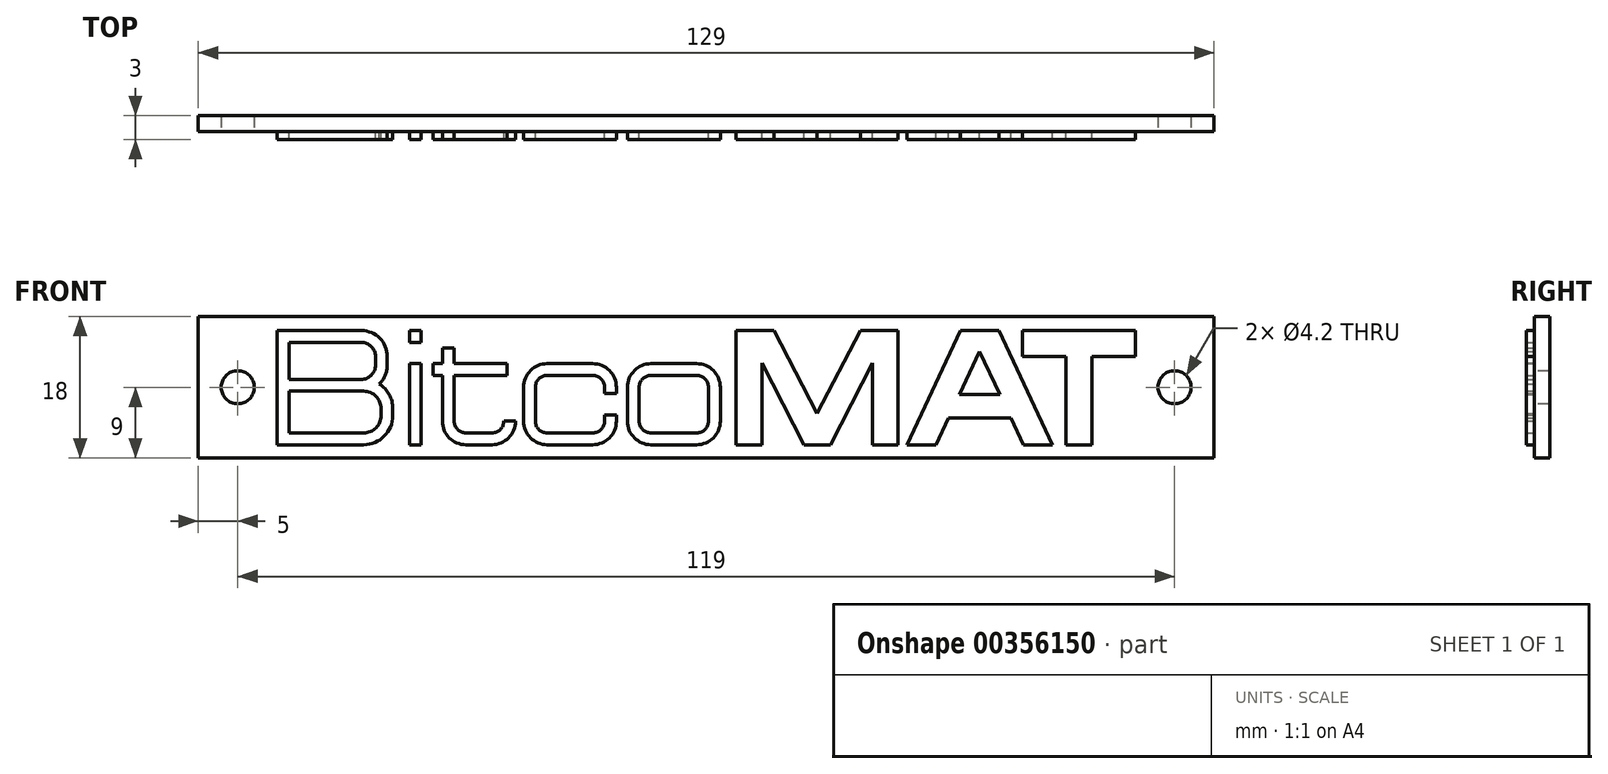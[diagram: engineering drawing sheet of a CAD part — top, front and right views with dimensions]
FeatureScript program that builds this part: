
annotation { "Feature Type Name" : "Feature", "Feature Type Description" : "" }
export const myFeature = defineFeature(function(context is Context, id is Id, definition is map)
    precondition{}
    {
        {
            var Q0;
            Q0=qCreatedBy(makeId("Front.planeOp"),FACE);
            var sketch = newSketch(context, id + "F0", { "sketchPlane" : qUnion([Q0])});
            skLineSegment(sketch, "E0.bottom", {"start": v(0, 0) * mm, "end": v(129, 0) * mm});
            skLineSegment(sketch, "E0.top", {"start": v(0, 18) * mm, "end": v(129, 18) * mm});
            skLineSegment(sketch, "E0.left", {"start": v(0, 0) * mm, "end": v(0, 18) * mm});
            skLineSegment(sketch, "E0.right", {"start": v(129, 0) * mm, "end": v(129, 18) * mm});
            skLineSegment(sketch, "E1", {"start": v(71.6, 1.7) * mm, "end": v(68.3, 1.7) * mm});
            skLineSegment(sketch, "E2", {"start": v(68.3, 1.7) * mm, "end": v(68.3, 16.2) * mm});
            skLineSegment(sketch, "E3", {"start": v(68.3, 16.2) * mm, "end": v(73.1, 16.2) * mm});
            skLineSegment(sketch, "E4", {"start": v(73.1, 16.2) * mm, "end": v(78.6, 5.7) * mm});
            skLineSegment(sketch, "E5", {"start": v(78.6, 5.7) * mm, "end": v(84.1, 16.2) * mm});
            skLineSegment(sketch, "E6", {"start": v(84.1, 16.2) * mm, "end": v(88.9, 16.2) * mm});
            skLineSegment(sketch, "E7", {"start": v(88.9, 16.2) * mm, "end": v(88.9, 1.7) * mm});
            skLineSegment(sketch, "E8", {"start": v(88.9, 1.7) * mm, "end": v(85.6, 1.7) * mm});
            skLineSegment(sketch, "E9", {"start": v(85.6, 1.7) * mm, "end": v(85.6, 12.1) * mm});
            skLineSegment(sketch, "E10", {"start": v(85.6, 12.1) * mm, "end": v(80.3, 1.7) * mm});
            skLineSegment(sketch, "E11", {"start": v(80.3, 1.7) * mm, "end": v(76.9, 1.7) * mm});
            skLineSegment(sketch, "E12", {"start": v(76.9, 1.7) * mm, "end": v(71.6, 12.1) * mm});
            skLineSegment(sketch, "E13", {"start": v(71.6, 12.1) * mm, "end": v(71.6, 1.7) * mm});
            skLineSegment(sketch, "E14", {"start": v(90, 1.7) * mm, "end": v(96.8, 16.2) * mm});
            skLineSegment(sketch, "E15", {"start": v(96.8, 16.2) * mm, "end": v(101.7, 16.2) * mm});
            skLineSegment(sketch, "E16", {"start": v(101.7, 16.2) * mm, "end": v(108.5, 1.7) * mm});
            skLineSegment(sketch, "E17", {"start": v(108.5, 1.7) * mm, "end": v(104.8, 1.7) * mm});
            skLineSegment(sketch, "E18", {"start": v(104.8, 1.7) * mm, "end": v(103.2, 5.1) * mm});
            skLineSegment(sketch, "E19", {"start": v(103.2, 5.1) * mm, "end": v(95.3, 5.1) * mm});
            skLineSegment(sketch, "E20", {"start": v(95.3, 5.1) * mm, "end": v(93.7, 1.7) * mm});
            skLineSegment(sketch, "E21", {"start": v(93.7, 1.7) * mm, "end": v(90, 1.7) * mm});
            skLineSegment(sketch, "E22", {"start": v(101.8, 8.1) * mm, "end": v(96.7, 8.1) * mm});
            skLineSegment(sketch, "E23", {"start": v(96.7, 8.1) * mm, "end": v(99.25, 13.55) * mm});
            skLineSegment(sketch, "E24", {"start": v(99.25, 13.55) * mm, "end": v(101.8, 8.1) * mm});
            skLineSegment(sketch, "E25", {"start": v(104.7, 16.2) * mm, "end": v(119, 16.2) * mm});
            skLineSegment(sketch, "E26", {"start": v(119, 16.2) * mm, "end": v(119, 12.9) * mm});
            skLineSegment(sketch, "E27", {"start": v(119, 12.9) * mm, "end": v(113.5, 12.9) * mm});
            skLineSegment(sketch, "E28", {"start": v(113.5, 12.9) * mm, "end": v(113.5, 1.7) * mm});
            skLineSegment(sketch, "E29", {"start": v(113.5, 1.7) * mm, "end": v(110.2, 1.7) * mm});
            skLineSegment(sketch, "E30", {"start": v(110.2, 1.7) * mm, "end": v(110.2, 12.9) * mm});
            skLineSegment(sketch, "E31", {"start": v(110.2, 12.9) * mm, "end": v(104.7, 12.9) * mm});
            skLineSegment(sketch, "E32", {"start": v(104.7, 12.9) * mm, "end": v(104.7, 16.2) * mm});
            skLineSegment(sketch, "E33.bottom", {"start": v(26.8, 16.2) * mm, "end": v(28.3, 16.2) * mm});
            skLineSegment(sketch, "E33.top", {"start": v(26.8, 14.7) * mm, "end": v(28.3, 14.7) * mm});
            skLineSegment(sketch, "E33.left", {"start": v(26.8, 16.2) * mm, "end": v(26.8, 14.7) * mm});
            skLineSegment(sketch, "E33.right", {"start": v(28.3, 16.2) * mm, "end": v(28.3, 14.7) * mm});
            skLineSegment(sketch, "E34.bottom", {"start": v(26.8, 12) * mm, "end": v(28.3, 12) * mm});
            skLineSegment(sketch, "E34.top", {"start": v(26.8, 1.7) * mm, "end": v(28.3, 1.7) * mm});
            skLineSegment(sketch, "E34.left", {"start": v(26.8, 12) * mm, "end": v(26.8, 1.7) * mm});
            skLineSegment(sketch, "E34.right", {"start": v(28.3, 12) * mm, "end": v(28.3, 1.7) * mm});
            skLineSegment(sketch, "E35", {"start": v(32.5, 4.7) * mm, "end": v(32.5, 10.5) * mm});
            skLineSegment(sketch, "E36", {"start": v(32.5, 10.5) * mm, "end": v(39.2, 10.5) * mm});
            skLineSegment(sketch, "E37", {"start": v(39.2, 10.5) * mm, "end": v(39.2, 12) * mm});
            skLineSegment(sketch, "E38", {"start": v(39.2, 12) * mm, "end": v(32.5, 12) * mm});
            skLineSegment(sketch, "E39", {"start": v(32.5, 12) * mm, "end": v(32.5, 14) * mm});
            skLineSegment(sketch, "E40", {"start": v(32.5, 14) * mm, "end": v(31, 14) * mm});
            skLineSegment(sketch, "E41", {"start": v(31, 14) * mm, "end": v(31, 12) * mm});
            skLineSegment(sketch, "E42", {"start": v(31, 12) * mm, "end": v(29.8, 12) * mm});
            skLineSegment(sketch, "E43", {"start": v(29.8, 12) * mm, "end": v(29.8, 10.5) * mm});
            skLineSegment(sketch, "E44", {"start": v(29.8, 10.5) * mm, "end": v(31, 10.5) * mm});
            skLineSegment(sketch, "E45", {"start": v(31, 10.5) * mm, "end": v(31, 4.7) * mm});
            skLineSegment(sketch, "E46", {"start": v(34, 3.2) * mm, "end": v(37.3, 3.2) * mm});
            skLineSegment(sketch, "E47", {"start": v(34, 1.7) * mm, "end": v(37.3, 1.7) * mm});
            skLineSegment(sketch, "E48", {"start": v(38.8, 4.7) * mm, "end": v(40.3, 4.7) * mm});
            skArc(sketch, "E49", {"start": v(32.5, 4.7) * mm, "mid": v(32.94, 3.64) * mm, "end": v(34, 3.2) * mm});
            skArc(sketch, "E50", {"start": v(31, 4.7) * mm, "mid": v(31.88, 2.58) * mm, "end": v(34, 1.7) * mm});
            skArc(sketch, "E51", {"start": v(37.3, 3.2) * mm, "mid": v(38.36, 3.64) * mm, "end": v(38.8, 4.7) * mm});
            skArc(sketch, "E52", {"start": v(37.3, 1.7) * mm, "mid": v(39.42, 2.58) * mm, "end": v(40.3, 4.7) * mm});
            skLineSegment(sketch, "E53", {"start": v(44.3, 10.5) * mm, "end": v(50.1, 10.5) * mm});
            skLineSegment(sketch, "E54", {"start": v(44.3, 12) * mm, "end": v(50.1, 12) * mm});
            skLineSegment(sketch, "E55", {"start": v(44.3, 3.2) * mm, "end": v(50.1, 3.2) * mm});
            skLineSegment(sketch, "E56", {"start": v(44.3, 1.7) * mm, "end": v(50.1, 1.7) * mm});
            skLineSegment(sketch, "E57", {"start": v(42.8, 9) * mm, "end": v(42.8, 4.7) * mm});
            skLineSegment(sketch, "E58", {"start": v(41.3, 9) * mm, "end": v(41.3, 4.7) * mm});
            skArc(sketch, "E59", {"start": v(44.3, 10.5) * mm, "mid": v(43.24, 10.06) * mm, "end": v(42.8, 9) * mm});
            skArc(sketch, "E60", {"start": v(44.3, 12) * mm, "mid": v(42.18, 11.12) * mm, "end": v(41.3, 9) * mm});
            skArc(sketch, "E61", {"start": v(51.6, 9) * mm, "mid": v(51.16, 10.06) * mm, "end": v(50.1, 10.5) * mm});
            skArc(sketch, "E62", {"start": v(53.1, 9) * mm, "mid": v(52.22, 11.12) * mm, "end": v(50.1, 12) * mm});
            skArc(sketch, "E63", {"start": v(42.8, 4.7) * mm, "mid": v(43.24, 3.64) * mm, "end": v(44.3, 3.2) * mm});
            skArc(sketch, "E64", {"start": v(41.3, 4.7) * mm, "mid": v(42.18, 2.58) * mm, "end": v(44.3, 1.7) * mm});
            skArc(sketch, "E65", {"start": v(50.1, 3.2) * mm, "mid": v(51.16, 3.64) * mm, "end": v(51.6, 4.7) * mm});
            skArc(sketch, "E66", {"start": v(50.1, 1.7) * mm, "mid": v(52.22, 2.58) * mm, "end": v(53.1, 4.7) * mm});
            skLineSegment(sketch, "E67", {"start": v(57.5, 10.5) * mm, "end": v(63.3, 10.5) * mm});
            skLineSegment(sketch, "E68", {"start": v(64.8, 9) * mm, "end": v(64.8, 4.7) * mm});
            skLineSegment(sketch, "E69", {"start": v(63.3, 3.2) * mm, "end": v(57.5, 3.2) * mm});
            skLineSegment(sketch, "E70", {"start": v(56, 4.7) * mm, "end": v(56, 9) * mm});
            skLineSegment(sketch, "E71", {"start": v(57.5, 12) * mm, "end": v(63.3, 12) * mm});
            skLineSegment(sketch, "E72", {"start": v(66.3, 9) * mm, "end": v(66.3, 4.7) * mm});
            skLineSegment(sketch, "E73", {"start": v(63.3, 1.7) * mm, "end": v(57.5, 1.7) * mm});
            skLineSegment(sketch, "E74", {"start": v(54.5, 9) * mm, "end": v(54.5, 4.7) * mm});
            skArc(sketch, "E75", {"start": v(57.5, 10.5) * mm, "mid": v(56.44, 10.06) * mm, "end": v(56, 9) * mm});
            skArc(sketch, "E76", {"start": v(57.5, 12) * mm, "mid": v(55.38, 11.12) * mm, "end": v(54.5, 9) * mm});
            skArc(sketch, "E77", {"start": v(64.8, 9) * mm, "mid": v(64.36, 10.06) * mm, "end": v(63.3, 10.5) * mm});
            skArc(sketch, "E78", {"start": v(66.3, 9) * mm, "mid": v(65.42, 11.12) * mm, "end": v(63.3, 12) * mm});
            skArc(sketch, "E79", {"start": v(63.3, 3.2) * mm, "mid": v(64.36, 3.64) * mm, "end": v(64.8, 4.7) * mm});
            skArc(sketch, "E80", {"start": v(63.3, 1.7) * mm, "mid": v(65.42, 2.58) * mm, "end": v(66.3, 4.7) * mm});
            skArc(sketch, "E81", {"start": v(56, 4.7) * mm, "mid": v(56.44, 3.64) * mm, "end": v(57.5, 3.2) * mm});
            skArc(sketch, "E82", {"start": v(54.5, 4.7) * mm, "mid": v(55.38, 2.58) * mm, "end": v(57.5, 1.7) * mm});
            skLineSegment(sketch, "E83", {"start": v(10, 16.2) * mm, "end": v(10, 1.7) * mm});
            skLineSegment(sketch, "E84", {"start": v(10, 1.7) * mm, "end": v(21, 1.7) * mm});
            skLineSegment(sketch, "E85", {"start": v(10, 16.2) * mm, "end": v(20.7, 16.2) * mm});
            skLineSegment(sketch, "E86", {"start": v(20.7, 14.7) * mm, "end": v(11.5, 14.7) * mm});
            skLineSegment(sketch, "E87", {"start": v(11.5, 14.7) * mm, "end": v(11.5, 10) * mm});
            skLineSegment(sketch, "E88", {"start": v(11.5, 10) * mm, "end": v(20.7, 10) * mm});
            skLineSegment(sketch, "E89", {"start": v(21, 8.5) * mm, "end": v(11.5, 8.5) * mm});
            skLineSegment(sketch, "E90", {"start": v(11.5, 8.5) * mm, "end": v(11.5, 3.2) * mm});
            skLineSegment(sketch, "E91", {"start": v(11.5, 3.2) * mm, "end": v(21, 3.2) * mm});
            skLineSegment(sketch, "E92", {"start": v(23.2, 6.3) * mm, "end": v(23.2, 5.4) * mm});
            skLineSegment(sketch, "E93", {"start": v(24.7, 6.3) * mm, "end": v(24.7, 5.4) * mm});
            skLineSegment(sketch, "E94", {"start": v(22.5, 12.9) * mm, "end": v(22.5, 11.8) * mm});
            skLineSegment(sketch, "E95", {"start": v(24, 12.9) * mm, "end": v(24, 11.8) * mm});
            skArc(sketch, "E96", {"start": v(22.5, 12.9) * mm, "mid": v(21.97, 14.17) * mm, "end": v(20.7, 14.7) * mm});
            skArc(sketch, "E97", {"start": v(24, 12.9) * mm, "mid": v(23.03, 15.23) * mm, "end": v(20.7, 16.2) * mm});
            skArc(sketch, "E98", {"start": v(20.7, 10) * mm, "mid": v(21.97, 10.53) * mm, "end": v(22.5, 11.8) * mm});
            skArc(sketch, "E99", {"start": v(23.2, 6.3) * mm, "mid": v(22.56, 7.86) * mm, "end": v(21, 8.5) * mm});
            skArc(sketch, "E100", {"start": v(21, 3.2) * mm, "mid": v(22.56, 3.84) * mm, "end": v(23.2, 5.4) * mm});
            skArc(sketch, "E101", {"start": v(21, 1.7) * mm, "mid": v(23.62, 2.78) * mm, "end": v(24.7, 5.4) * mm});
            skArc(sketch, "E102", {"start": v(24.7, 6.3) * mm, "mid": v(24.24, 8.08) * mm, "end": v(22.99, 9.42) * mm});
            skArc(sketch, "E103", {"start": v(22.99, 9.42) * mm, "mid": v(23.74, 10.5) * mm, "end": v(24, 11.8) * mm});
            skLineSegment(sketch, "E104", {"start": v(51.6, 4.7) * mm, "end": v(51.6, 5.5) * mm});
            skLineSegment(sketch, "E105", {"start": v(51.6, 5.5) * mm, "end": v(53.1, 5.5) * mm});
            skLineSegment(sketch, "E106", {"start": v(53.1, 5.5) * mm, "end": v(53.1, 4.7) * mm});
            skLineSegment(sketch, "E107", {"start": v(51.6, 9) * mm, "end": v(51.6, 8.2) * mm});
            skLineSegment(sketch, "E108", {"start": v(51.6, 8.2) * mm, "end": v(53.1, 8.2) * mm});
            skLineSegment(sketch, "E109", {"start": v(53.1, 8.2) * mm, "end": v(53.1, 9) * mm});
            skCircle(sketch, "E110", {"center": v(124, 9) * mm, "radius": 2.1 * mm});
            skCircle(sketch, "E111", {"center": v(5, 9) * mm, "radius": 2.1 * mm});
            skSolve(sketch);
        }
        {
            var Q0;
            Q0=makeQuery(id+"F0.imprint","IMPRINT",FACE,{"disambiguationData":[TD([[makeQuery(id+"F0.imprint","IMPRINT",EDGE,{"derivedFrom":sQuery(id+"F0.wireOp",EDGE,"E0.bottom")}),1.0]])]});
            var Q1;
            Q1=makeQuery(id+"F0.imprint","IMPRINT",FACE,{"disambiguationData":[TD([[makeQuery(id+"F0.imprint","IMPRINT",EDGE,{"derivedFrom":sQuery(id+"F0.wireOp",EDGE,"E25")}),-1.0]])]});
            var Q2;
            Q2=makeQuery(id+"F0.imprint","IMPRINT",FACE,{"disambiguationData":[TD([[makeQuery(id+"F0.imprint","IMPRINT",EDGE,{"derivedFrom":sQuery(id+"F0.wireOp",EDGE,"E1")}),-1.0]])]});
            var Q3;
            Q3=makeQuery(id+"F0.imprint","IMPRINT",FACE,{"disambiguationData":[TD([[makeQuery(id+"F0.imprint","IMPRINT",EDGE,{"derivedFrom":sQuery(id+"F0.wireOp",EDGE,"E22")}),-1.0]])]});
            var Q4;
            Q4=makeQuery(id+"F0.imprint","IMPRINT",FACE,{"disambiguationData":[TD([[makeQuery(id+"F0.imprint","IMPRINT",EDGE,{"derivedFrom":sQuery(id+"F0.wireOp",EDGE,"E83")}),1.0]])]});
            var Q5;
            Q5=makeQuery(id+"F0.imprint","IMPRINT",FACE,{"disambiguationData":[TD([[makeQuery(id+"F0.imprint","IMPRINT",EDGE,{"derivedFrom":sQuery(id+"F0.wireOp",EDGE,"E35")}),1.0]])]});
            var Q6;
            Q6=makeQuery(id+"F0.imprint","IMPRINT",FACE,{"disambiguationData":[TD([[makeQuery(id+"F0.imprint","IMPRINT",EDGE,{"derivedFrom":sQuery(id+"F0.wireOp",EDGE,"E53")}),1.0]])]});
            var Q7;
            Q7=makeQuery(id+"F0.imprint","IMPRINT",FACE,{"disambiguationData":[TD([[makeQuery(id+"F0.imprint","IMPRINT",EDGE,{"derivedFrom":sQuery(id+"F0.wireOp",EDGE,"E67")}),1.0]])]});
            var Q8;
            Q8=makeQuery(id+"F0.imprint","IMPRINT",FACE,{"disambiguationData":[TD([[makeQuery(id+"F0.imprint","IMPRINT",EDGE,{"derivedFrom":sQuery(id+"F0.wireOp",EDGE,"E14")}),-1.0]])]});
            var Q9;
            Q9=makeQuery(id+"F0.imprint","IMPRINT",FACE,{"disambiguationData":[TD([[makeQuery(id+"F0.imprint","IMPRINT",EDGE,{"derivedFrom":sQuery(id+"F0.wireOp",EDGE,"E34.bottom")}),-1.0]])]});
            var Q10;
            Q10=makeQuery(id+"F0.imprint","IMPRINT",FACE,{"disambiguationData":[TD([[makeQuery(id+"F0.imprint","IMPRINT",EDGE,{"derivedFrom":sQuery(id+"F0.wireOp",EDGE,"E89")}),1.0]])]});
            var Q11;
            Q11=makeQuery(id+"F0.imprint","IMPRINT",FACE,{"disambiguationData":[TD([[makeQuery(id+"F0.imprint","IMPRINT",EDGE,{"derivedFrom":sQuery(id+"F0.wireOp",EDGE,"E67")}),-1.0]])]});
            var Q12;
            Q12=makeQuery(id+"F0.imprint","IMPRINT",FACE,{"disambiguationData":[TD([[makeQuery(id+"F0.imprint","IMPRINT",EDGE,{"derivedFrom":sQuery(id+"F0.wireOp",EDGE,"E86")}),1.0]])]});
            var Q13;
            Q13=makeQuery(id+"F0.imprint","IMPRINT",FACE,{"disambiguationData":[TD([[makeQuery(id+"F0.imprint","IMPRINT",EDGE,{"derivedFrom":sQuery(id+"F0.wireOp",EDGE,"E33.bottom")}),-1.0]])]});
            extrude(context, id + "F1", {"entities" : qUnion([Q0, Q1, Q2, Q3, Q4, Q5, Q6, Q7, Q8, Q9, Q10, Q11, Q12, Q13]), "oppositeDirection" : true, "depth" : 2 * mm, "offsetDistance" : 25 * mm});
        }
        {
            var Q0;
            Q0=makeQuery(id+"F0.imprint","IMPRINT",FACE,{"disambiguationData":[TD([[makeQuery(id+"F0.imprint","IMPRINT",EDGE,{"derivedFrom":sQuery(id+"F0.wireOp",EDGE,"E83")}),1.0]])]});
            var Q1;
            Q1=makeQuery(id+"F0.imprint","IMPRINT",FACE,{"disambiguationData":[TD([[makeQuery(id+"F0.imprint","IMPRINT",EDGE,{"derivedFrom":sQuery(id+"F0.wireOp",EDGE,"E34.bottom")}),-1.0]])]});
            var Q2;
            Q2=makeQuery(id+"F0.imprint","IMPRINT",FACE,{"disambiguationData":[TD([[makeQuery(id+"F0.imprint","IMPRINT",EDGE,{"derivedFrom":sQuery(id+"F0.wireOp",EDGE,"E33.bottom")}),-1.0]])]});
            var Q3;
            Q3=makeQuery(id+"F0.imprint","IMPRINT",FACE,{"disambiguationData":[TD([[makeQuery(id+"F0.imprint","IMPRINT",EDGE,{"derivedFrom":sQuery(id+"F0.wireOp",EDGE,"E35")}),1.0]])]});
            var Q4;
            Q4=makeQuery(id+"F0.imprint","IMPRINT",FACE,{"disambiguationData":[TD([[makeQuery(id+"F0.imprint","IMPRINT",EDGE,{"derivedFrom":sQuery(id+"F0.wireOp",EDGE,"E53")}),1.0]])]});
            var Q5;
            Q5=makeQuery(id+"F0.imprint","IMPRINT",FACE,{"disambiguationData":[TD([[makeQuery(id+"F0.imprint","IMPRINT",EDGE,{"derivedFrom":sQuery(id+"F0.wireOp",EDGE,"E67")}),1.0]])]});
            var Q6;
            Q6=makeQuery(id+"F0.imprint","IMPRINT",FACE,{"disambiguationData":[TD([[makeQuery(id+"F0.imprint","IMPRINT",EDGE,{"derivedFrom":sQuery(id+"F0.wireOp",EDGE,"E1")}),-1.0]])]});
            var Q7;
            Q7=makeQuery(id+"F0.imprint","IMPRINT",FACE,{"disambiguationData":[TD([[makeQuery(id+"F0.imprint","IMPRINT",EDGE,{"derivedFrom":sQuery(id+"F0.wireOp",EDGE,"E14")}),-1.0]])]});
            var Q8;
            Q8=makeQuery(id+"F0.imprint","IMPRINT",FACE,{"disambiguationData":[TD([[makeQuery(id+"F0.imprint","IMPRINT",EDGE,{"derivedFrom":sQuery(id+"F0.wireOp",EDGE,"E25")}),-1.0]])]});
            extrude(context, id + "F2", {"entities" : qUnion([Q0, Q1, Q2, Q3, Q4, Q5, Q6, Q7, Q8]), "operationType" : NewBodyOperationType.ADD, "depth" : 1 * mm, "offsetDistance" : 25 * mm});
        }
    });
